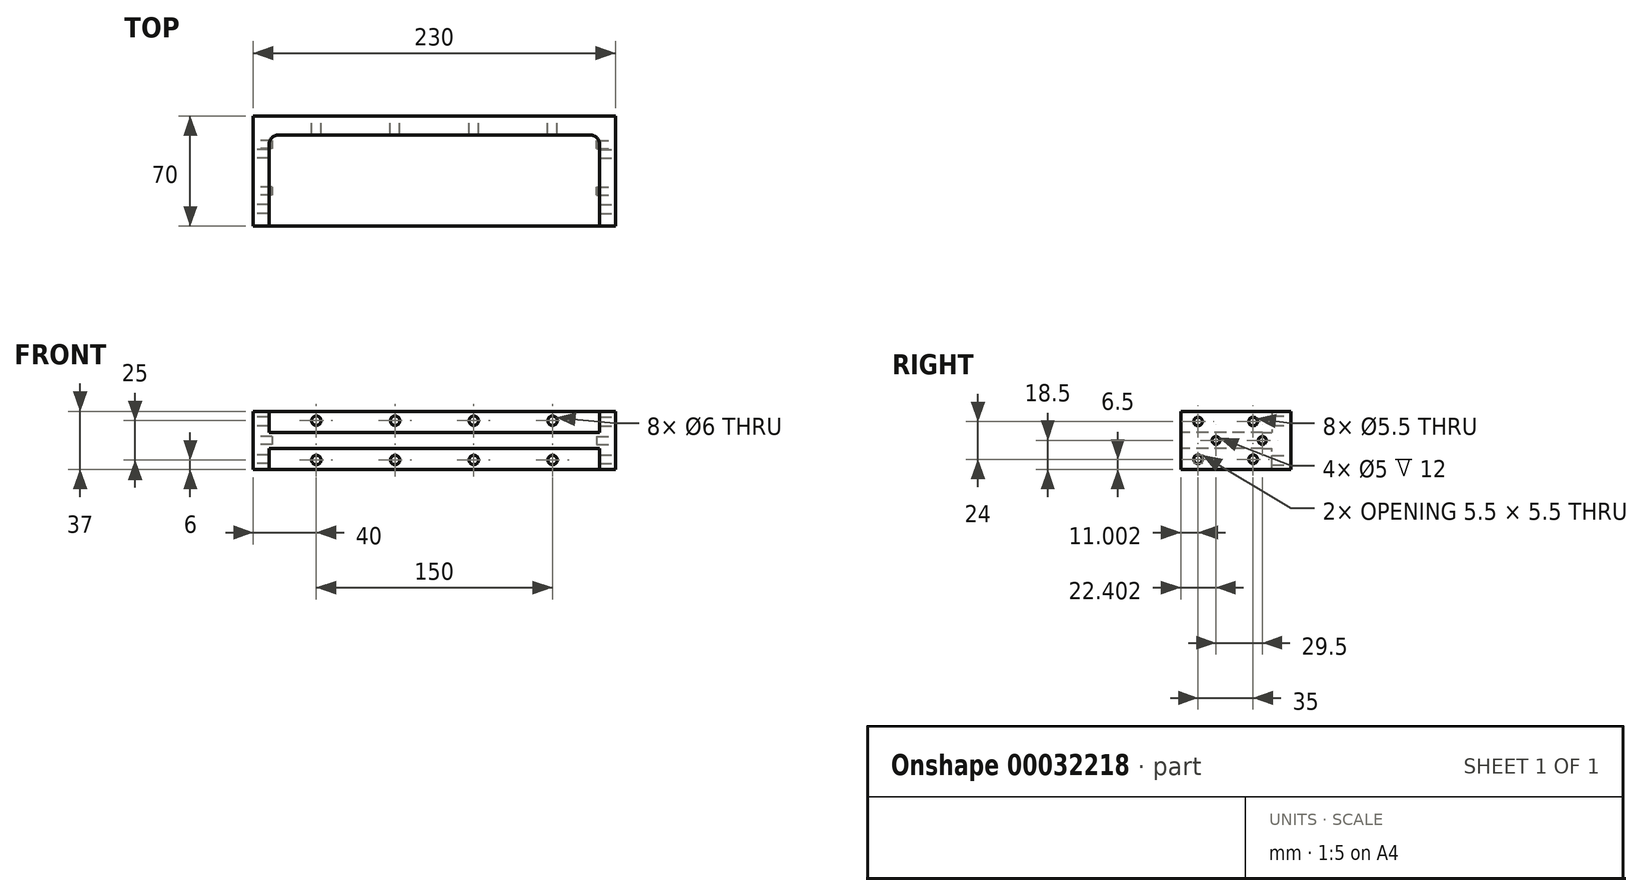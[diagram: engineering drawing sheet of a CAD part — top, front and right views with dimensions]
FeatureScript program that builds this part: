
annotation { "Feature Type Name" : "Feature", "Feature Type Description" : "" }
export const myFeature = defineFeature(function(context is Context, id is Id, definition is map)
    precondition{}
    {
        {
            var Q0;
            Q0=qCreatedBy(makeId("Top.planeOp"),FACE);
            var sketch = newSketch(context, id + "F0", { "sketchPlane" : qUnion([Q0])});
            skLineSegment(sketch, "E0.bottom", {"start": v(-115, 38.58) * mm, "end": v(0, 38.58) * mm});
            skLineSegment(sketch, "E0.top", {"start": v(-115, -31.42) * mm, "end": v(0, -31.42) * mm});
            skLineSegment(sketch, "E0.left", {"start": v(-115, 38.58) * mm, "end": v(-115, -31.42) * mm});
            skLineSegment(sketch, "E0.right", {"start": v(0, 38.58) * mm, "end": v(0, -31.42) * mm});
            skSolve(sketch);
        }
        {
            var Q0;
            Q0 = qSketchRegion(id + "F0", true);
            extrude(context, id + "F1", {"entities" : qUnion([Q0]), "depth" : 37 * mm});
        }
        {
            var Q0;
            Q0=makeQuery(id+"F1.opExtrude","SWEPT_FACE",FACE,{"disambiguationData":[OSD([sQuery(id+"F0.wireOp",EDGE,"E0.left")])]});
            var sketch = newSketch(context, id + "F2", { "sketchPlane" : qUnion([Q0])});
            skCircle(sketch, "E1", {"center": v(-14.58, 30.5) * mm, "radius": 2.75 * mm});
            skCircle(sketch, "E2", {"center": v(-14.58, 6.5) * mm, "radius": 2.75 * mm});
            skCircle(sketch, "E3", {"center": v(20.42, 6.5) * mm, "radius": 2.75 * mm});
            skCircle(sketch, "E4", {"center": v(20.42, 30.5) * mm, "radius": 2.75 * mm});
            skCircle(sketch, "E5", {"center": v(-20.48, 18.5) * mm, "radius": 2.5 * mm});
            skCircle(sketch, "E6", {"center": v(9.02, 18.5) * mm, "radius": 2.5 * mm});
            skSolve(sketch);
        }
        {
            var Q0;
            Q0 = qSketchRegion(id + "F2", true);
            extrude(context, id + "F3", {"entities" : qUnion([Q0]), "operationType" : NewBodyOperationType.REMOVE, "oppositeDirection" : true, "depth" : 12 * mm});
        }
        {
            var Q0;
            Q0=makeQuery(id+"F1.opExtrude","SWEPT_FACE",FACE,{"disambiguationData":[OSD([sQuery(id+"F0.wireOp",EDGE,"E0.top")])]});
            var sketch = newSketch(context, id + "F4", { "sketchPlane" : qUnion([Q0])});
            skLineSegment(sketch, "E7.bottom", {"start": v(0, 0) * mm, "end": v(-105, 0) * mm});
            skLineSegment(sketch, "E7.top", {"start": v(0, 13.5) * mm, "end": v(-105, 13.5) * mm});
            skLineSegment(sketch, "E7.left", {"start": v(0, 0) * mm, "end": v(0, 13.5) * mm});
            skLineSegment(sketch, "E7.right", {"start": v(-105, 0) * mm, "end": v(-105, 13.5) * mm});
            skLineSegment(sketch, "E8.bottom", {"start": v(0, 37) * mm, "end": v(-105, 37) * mm});
            skLineSegment(sketch, "E8.top", {"start": v(0, 23.5) * mm, "end": v(-105, 23.5) * mm});
            skLineSegment(sketch, "E8.left", {"start": v(0, 37) * mm, "end": v(0, 23.5) * mm});
            skLineSegment(sketch, "E8.right", {"start": v(-105, 37) * mm, "end": v(-105, 23.5) * mm});
            skSolve(sketch);
        }
        {
            var Q0;
            Q0 = qSketchRegion(id + "F4", true);
            extrude(context, id + "F5", {"entities" : qUnion([Q0]), "operationType" : NewBodyOperationType.REMOVE, "oppositeDirection" : true, "depth" : 58 * mm});
        }
        {
            var Q0;
            Q0=makeQuery(id+"F1.opExtrude","SWEPT_FACE",FACE,{"disambiguationData":[OSD([sQuery(id+"F0.wireOp",EDGE,"E0.bottom")])]});
            var sketch = newSketch(context, id + "F6", { "sketchPlane" : qUnion([Q0])});
            skCircle(sketch, "E9", {"center": v(75, 6) * mm, "radius": 3 * mm});
            skCircle(sketch, "E10", {"center": v(75, 31) * mm, "radius": 3 * mm});
            skCircle(sketch, "E11", {"center": v(25, 31) * mm, "radius": 3 * mm});
            skCircle(sketch, "E12", {"center": v(25, 6) * mm, "radius": 3 * mm});
            skSolve(sketch);
        }
        {
            var Q0;
            Q0 = qSketchRegion(id + "F6", true);
            extrude(context, id + "F7", {"entities" : qUnion([Q0]), "operationType" : NewBodyOperationType.REMOVE, "endBound" : BoundingType.THROUGH_ALL, "oppositeDirection" : true, "depth" : 25 * mm});
        }
        {
            var Q0;
            Q0=makeQuery(id+"F1.opExtrude","SWEPT_BODY",BODY,{"disambiguationData":[OSD([sQuery(id+"F0.wireOp",EDGE,"E0.bottom"),sQuery(id+"F0.wireOp",EDGE,"E0.top"),sQuery(id+"F0.wireOp",EDGE,"E0.left"),sQuery(id+"F0.wireOp",EDGE,"E0.right")])]});
            var Q1;
            Q1=qCreatedBy(makeId("Right.planeOp"),FACE);
            mirror(context, id + "F8", {"operationType" : NewBodyOperationType.ADD, "entities" : qUnion([Q0]), "mirrorPlane" : qUnion([Q1])});
        }
        {
            var Q0;
            Q0=makeQuery(id+"F5.boolean.opBoolean","COPY",EDGE,{"derivedFrom":makeQuery(id+"F5.opExtrude","CAP_EDGE",EDGE,{"disambiguationData":[OSD([sQuery(id+"F4.wireOp",EDGE,"E7.right")])],"isStart":false})});
            var Q1;
            Q1=makeQuery(id+"F8.opPattern","COPY",EDGE,{"derivedFrom":makeQuery(id+"F5.boolean.opBoolean","COPY",EDGE,{"derivedFrom":makeQuery(id+"F5.opExtrude","CAP_EDGE",EDGE,{"disambiguationData":[OSD([sQuery(id+"F4.wireOp",EDGE,"E7.right")])],"isStart":false})}),"instanceName":"1"});
            var Q2;
            Q2=makeQuery(id+"F5.boolean.opBoolean","COPY",EDGE,{"derivedFrom":makeQuery(id+"F5.opExtrude","CAP_EDGE",EDGE,{"disambiguationData":[OSD([sQuery(id+"F4.wireOp",EDGE,"E8.right")])],"isStart":false})});
            var Q3;
            Q3=makeQuery(id+"F8.opPattern","COPY",EDGE,{"derivedFrom":makeQuery(id+"F5.boolean.opBoolean","COPY",EDGE,{"derivedFrom":makeQuery(id+"F5.opExtrude","CAP_EDGE",EDGE,{"disambiguationData":[OSD([sQuery(id+"F4.wireOp",EDGE,"E8.right")])],"isStart":false})}),"instanceName":"1"});
            fillet(context, id + "F9", {"entities" : qUnion([Q0, Q1, Q2, Q3]), "radius" : 6 * mm, "tangentPropagation" : true, "allowEdgeOverflow" : false});
        }
    });
